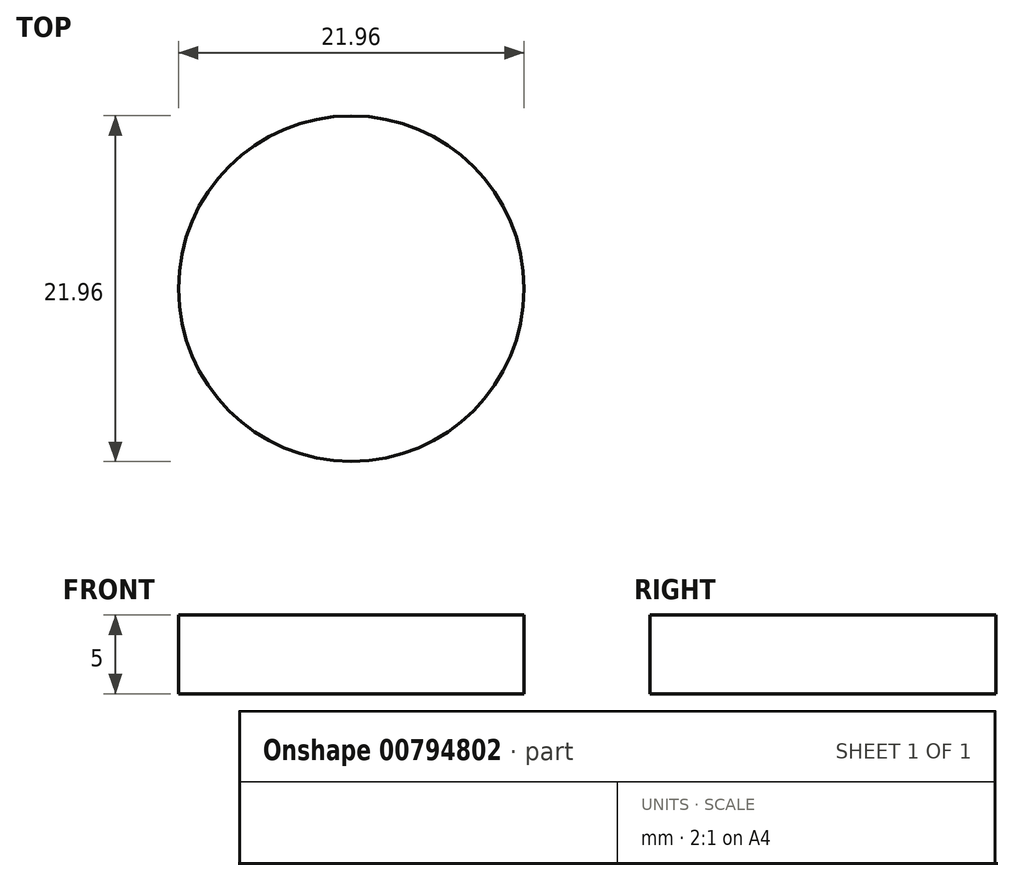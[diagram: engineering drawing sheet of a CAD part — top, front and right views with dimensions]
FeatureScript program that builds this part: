
annotation { "Feature Type Name" : "Feature", "Feature Type Description" : "" }
export const myFeature = defineFeature(function(context is Context, id is Id, definition is map)
    precondition{}
    {
        {
            var Q0;
            Q0=qCreatedBy(makeId("Top.planeOp"),FACE);
            var sketch = newSketch(context, id + "F0", { "sketchPlane" : qUnion([Q0])});
            skCircle(sketch, "E0", {"center": v(0, 0) * mm, "radius": 10.97 * mm});
            skSolve(sketch);
        }
        {
            var Q0;
            Q0 = qSketchRegion(id + "F0", true);
            extrude(context, id + "F1", {"entities" : qUnion([Q0]), "depth" : 5 * mm, "offsetDistance" : 25 * mm});
        }
    });
